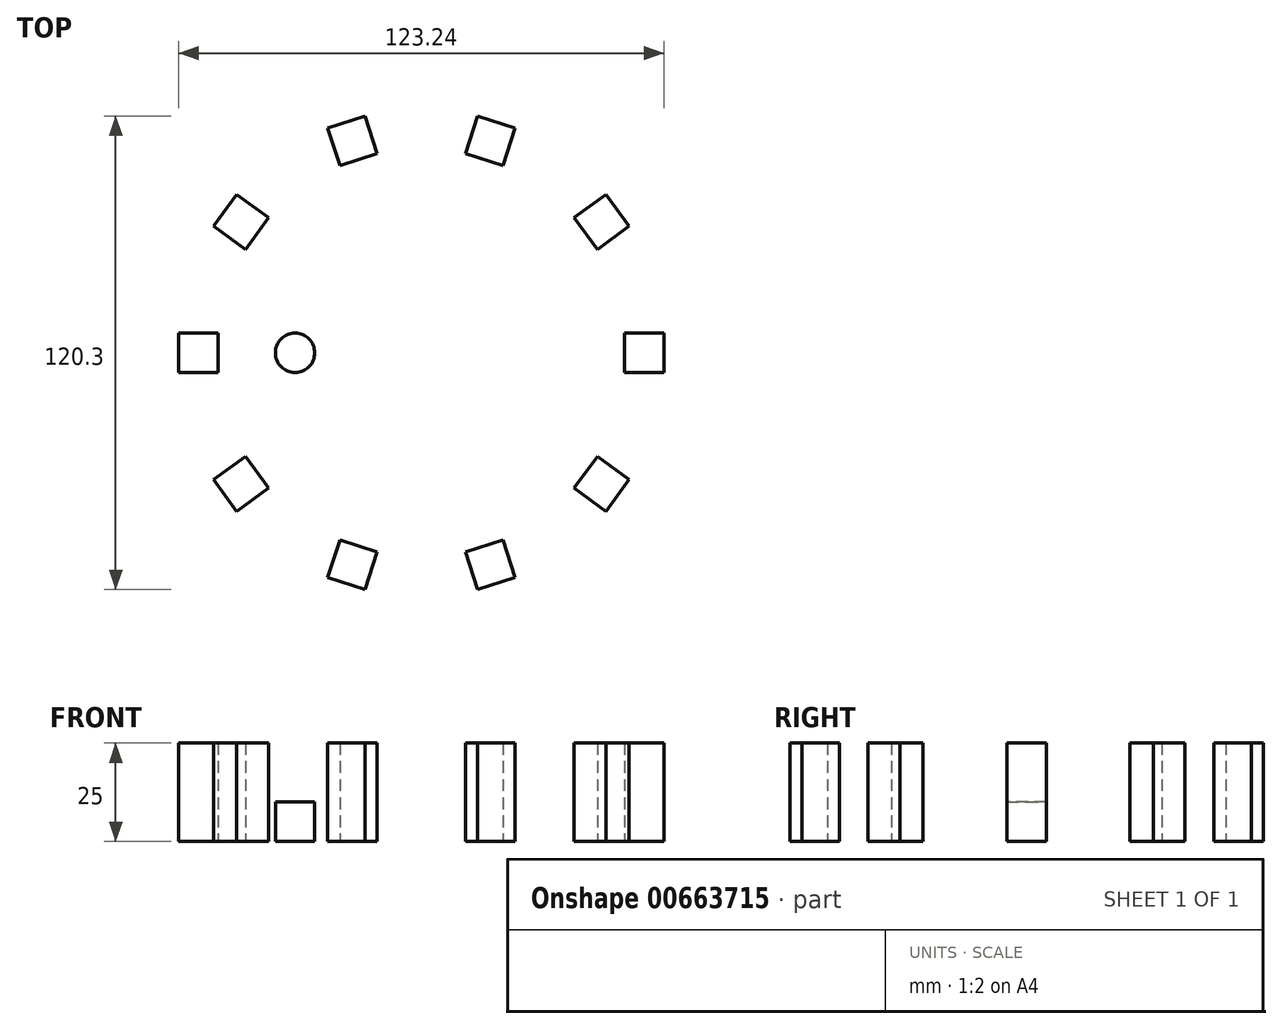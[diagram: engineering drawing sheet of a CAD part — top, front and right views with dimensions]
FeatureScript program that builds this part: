
annotation { "Feature Type Name" : "Feature", "Feature Type Description" : "" }
export const myFeature = defineFeature(function(context is Context, id is Id, definition is map)
    precondition{}
    {
        {
            var Q0;
            Q0=qCreatedBy(makeId("Top.planeOp"),FACE);
            var sketch = newSketch(context, id + "F0", { "sketchPlane" : qUnion([Q0])});
            skLineSegment(sketch, "E0.bottom", {"start": v(-51.62, -5) * mm, "end": v(-61.62, -5) * mm});
            skLineSegment(sketch, "E0.top", {"start": v(-51.62, 5) * mm, "end": v(-61.62, 5) * mm});
            skLineSegment(sketch, "E0.left", {"start": v(-51.62, -5) * mm, "end": v(-51.62, 5) * mm});
            skLineSegment(sketch, "E0.right", {"start": v(-61.62, -5) * mm, "end": v(-61.62, 5) * mm});
            skPoint(sketch, "E0.middle", {"position": v(-56.62, 0) * mm});
            skSolve(sketch);
        }
        {
            var Q0;
            Q0 = qSketchRegion(id + "F0", true);
            extrude(context, id + "F1", {"entities" : qUnion([Q0]), "depth" : 25 * mm, "offsetDistance" : 25 * mm});
        }
        {
            var Q0;
            Q0=qCreatedBy(makeId("Right.planeOp"),FACE);
            var sketch = newSketch(context, id + "F2", { "sketchPlane" : qUnion([Q0])});
            skLineSegment(sketch, "E1", {"start": v(0, 0) * mm, "end": v(0, 39.18) * mm});
            skSolve(sketch);
        }
        {
            var Q0;
            Q0=makeQuery(id+"F1.opExtrude","SWEPT_BODY",BODY,{"disambiguationData":[OSD([sQuery(id+"F0.wireOp",EDGE,"E0.bottom"),sQuery(id+"F0.wireOp",EDGE,"E0.top"),sQuery(id+"F0.wireOp",EDGE,"E0.left"),sQuery(id+"F0.wireOp",EDGE,"E0.right")])]});
            var Q1;
            Q1=sQuery(id+"F2.wireOp",EDGE,"E1");
            circularPattern(context, id + "F3", {"entities" : qUnion([Q0]), "axis" : qUnion([Q1]), "angle" : 360 * degree, "instanceCount" : 10, "equalSpace" : true});
        }
        {
            var Q0;
            Q0=qCreatedBy(makeId("Top.planeOp"),FACE);
            var sketch = newSketch(context, id + "F4", { "sketchPlane" : qUnion([Q0])});
            skCircle(sketch, "E2", {"center": v(-32.1, 0) * mm, "radius": 5 * mm});
            skSolve(sketch);
        }
        {
            var Q0;
            Q0 = qSketchRegion(id + "F4", true);
            extrude(context, id + "F5", {"entities" : qUnion([Q0]), "depth" : 10 * mm, "offsetDistance" : 25 * mm});
        }
    });
